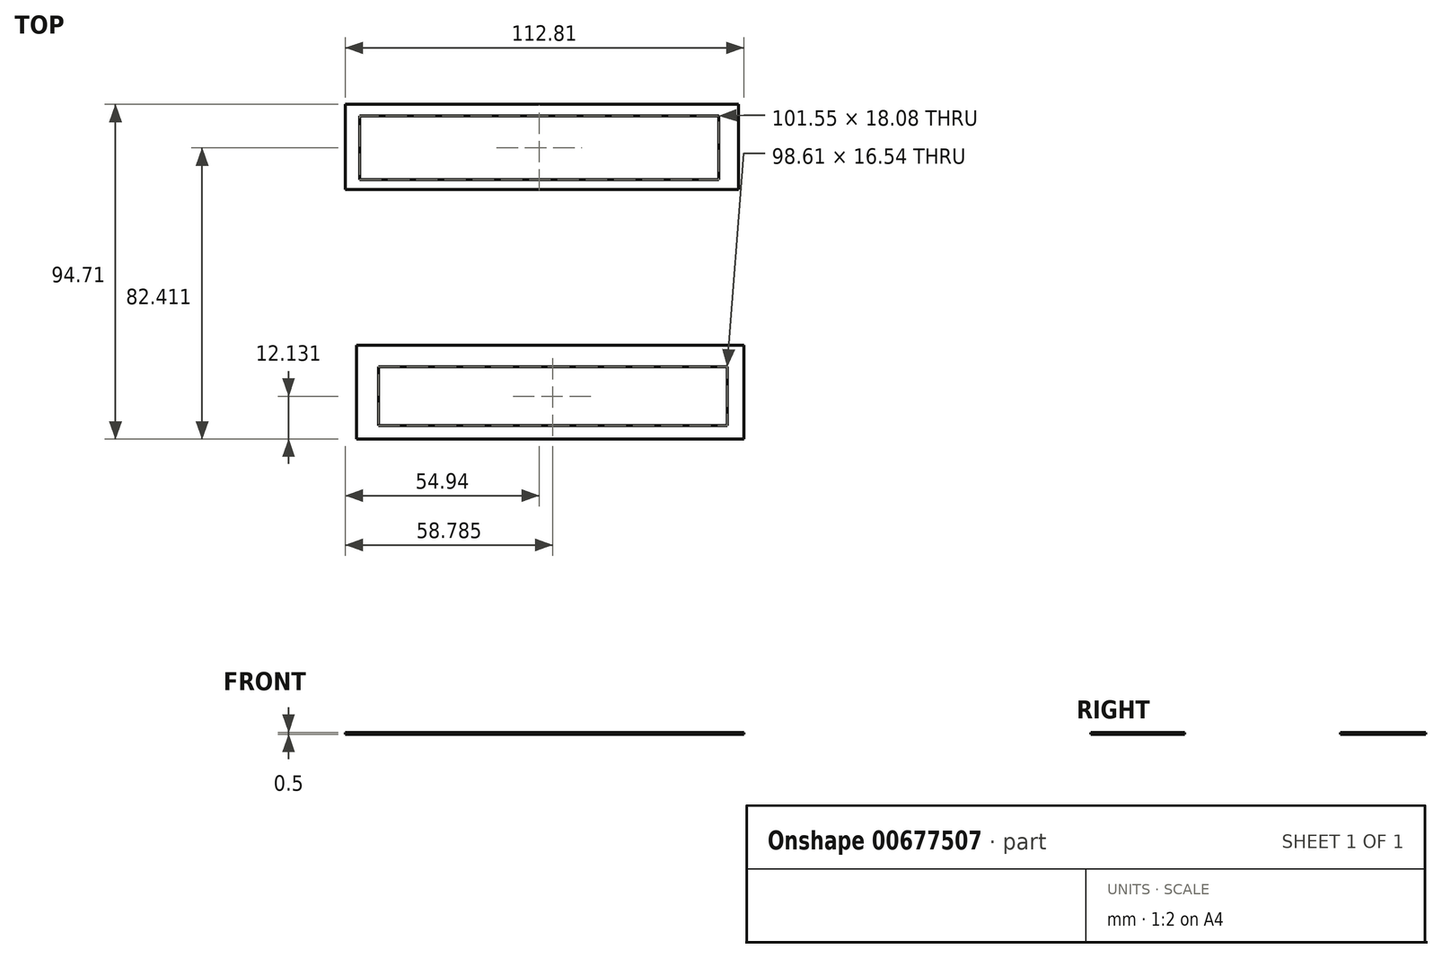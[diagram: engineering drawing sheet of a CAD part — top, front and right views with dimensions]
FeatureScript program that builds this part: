
annotation { "Feature Type Name" : "Feature", "Feature Type Description" : "" }
export const myFeature = defineFeature(function(context is Context, id is Id, definition is map)
    precondition{}
    {
        {
            var Q0;
            Q0=qCreatedBy(makeId("Top.planeOp"),FACE);
            var sketch = newSketch(context, id + "F0", { "sketchPlane" : qUnion([Q0])});
            skLineSegment(sketch, "E0.bottom", {"start": v(-52.43, 41.44) * mm, "end": v(58.84, 41.44) * mm});
            skLineSegment(sketch, "E0.top", {"start": v(-52.43, 17.29) * mm, "end": v(58.84, 17.29) * mm});
            skLineSegment(sketch, "E0.left", {"start": v(-52.43, 41.44) * mm, "end": v(-52.43, 17.29) * mm});
            skLineSegment(sketch, "E0.right", {"start": v(58.84, 41.44) * mm, "end": v(58.84, 17.29) * mm});
            skLineSegment(sketch, "E1.bottom", {"start": v(-48.27, 38.18) * mm, "end": v(53.29, 38.18) * mm});
            skLineSegment(sketch, "E1.top", {"start": v(-48.27, 20.1) * mm, "end": v(53.29, 20.1) * mm});
            skLineSegment(sketch, "E1.left", {"start": v(-48.27, 38.18) * mm, "end": v(-48.27, 20.1) * mm});
            skLineSegment(sketch, "E1.right", {"start": v(53.29, 38.18) * mm, "end": v(53.29, 20.1) * mm});
            skSolve(sketch);
        }
        {
            var Q0;
            Q0=qCreatedBy(makeId("Top.planeOp"),FACE);
            var sketch = newSketch(context, id + "F1", { "sketchPlane" : qUnion([Q0])});
            skLineSegment(sketch, "E2.bottom", {"start": v(-49.25, -26.73) * mm, "end": v(60.38, -26.73) * mm});
            skLineSegment(sketch, "E2.top", {"start": v(-49.25, -53.27) * mm, "end": v(60.38, -53.27) * mm});
            skLineSegment(sketch, "E2.left", {"start": v(-49.25, -26.73) * mm, "end": v(-49.25, -53.27) * mm});
            skLineSegment(sketch, "E2.right", {"start": v(60.38, -26.73) * mm, "end": v(60.38, -53.27) * mm});
            skLineSegment(sketch, "E3.bottom", {"start": v(-42.95, -32.87) * mm, "end": v(55.66, -32.87) * mm});
            skLineSegment(sketch, "E3.top", {"start": v(-42.95, -49.4) * mm, "end": v(55.66, -49.4) * mm});
            skLineSegment(sketch, "E3.left", {"start": v(-42.95, -32.87) * mm, "end": v(-42.95, -49.4) * mm});
            skLineSegment(sketch, "E3.right", {"start": v(55.66, -32.87) * mm, "end": v(55.66, -49.4) * mm});
            skSolve(sketch);
        }
        {
            var Q0;
            Q0 = qSketchRegion(id + "F0", true);
            var Q1;
            Q1=makeQuery(id+"F0.imprint","IMPRINT",FACE,{"disambiguationData":[TD([[makeQuery(id+"F0.imprint","IMPRINT",EDGE,{"derivedFrom":sQuery(id+"F0.wireOp",EDGE,"E0.bottom")}),-1.0]])]});
            var Q2;
            Q2=makeQuery(id+"F1.imprint","IMPRINT",FACE,{"disambiguationData":[TD([[makeQuery(id+"F1.imprint","IMPRINT",EDGE,{"derivedFrom":sQuery(id+"F1.wireOp",EDGE,"E2.bottom")}),-1.0]])]});
            extrude(context, id + "F2", {"entities" : qUnion([Q0, Q1, Q2]), "depth" : 0.5 * mm, "offsetDistance" : 25 * mm});
        }
    });
